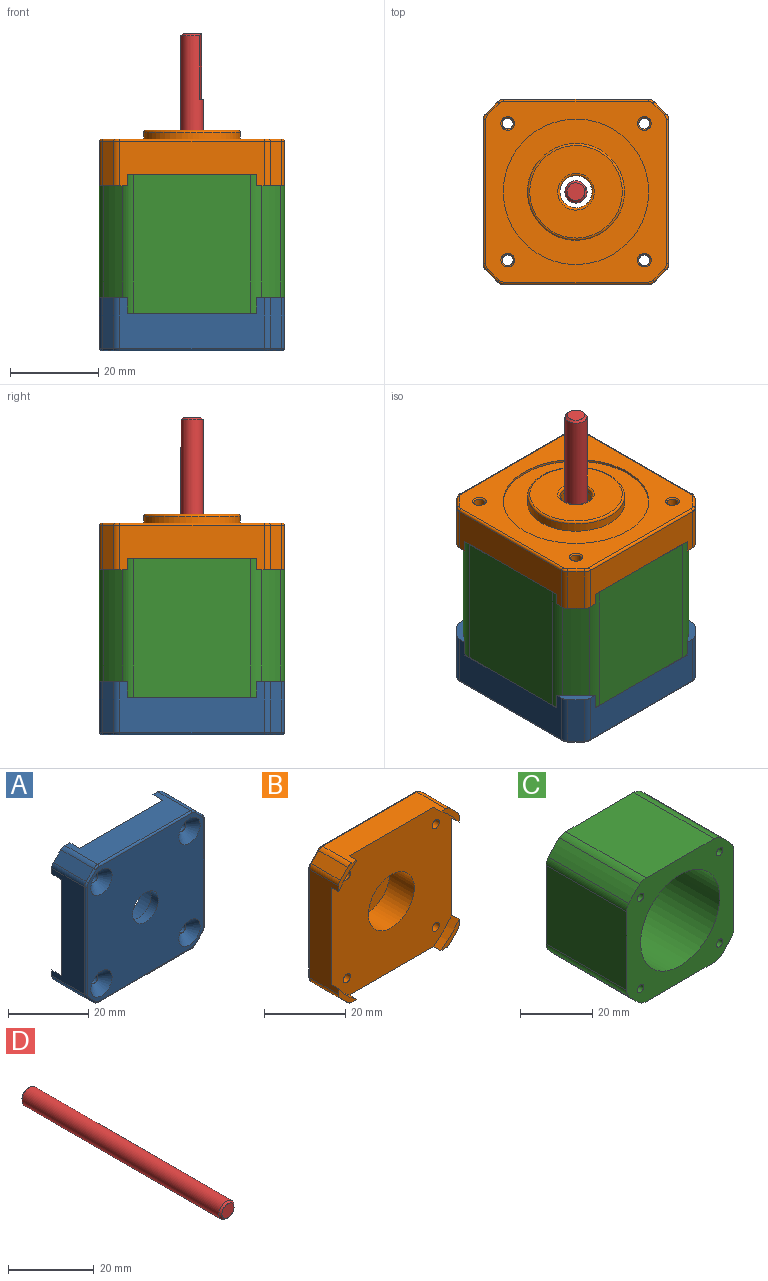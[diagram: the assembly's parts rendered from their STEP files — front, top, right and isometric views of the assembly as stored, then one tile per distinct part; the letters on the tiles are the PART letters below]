
ASSEMBLY  parts=4 mates=8
PART A: 53 faces, bbox 42.3x12x42.3 mm
  f0: cylinder r=4.5mm len=9mm, axis (0,-1,0), area 70.7mm2, adj f10,f28
  f1: plane 32.74x11.5mm, normal (0,0,1), area 274.1mm2, adj f9,f11,f13,f14,f16,f30,f31,f50
  f2: plane 32.74x11.5mm, normal (1,0,0), area 274.1mm2, adj f9,f11,f13,f20,f22,f29,f36,f42
  f3: plane 32.74x11.5mm, normal (0,0,-1), area 274.1mm2, adj f9,f17,f19,f20,f22,f34,f35,f39
  f4: plane 32.74x11.5mm, normal (-1,0,0), area 274.1mm2, adj f9,f14,f16,f17,f19,f32,f33,f47
  f5: cylinder r=1.25mm len=6mm, axis (0,-1,0), area 47.1mm2, adj f9,f26
  f6: cylinder r=1.25mm len=6mm, axis (0,-1,0), area 47.1mm2, adj f9,f25
  f7: cylinder r=1.25mm len=6mm, axis (0,-1,0), area 47.1mm2, adj f9,f24
  f8: cylinder r=1.25mm len=6mm, axis (0,-1,0), area 47.1mm2, adj f9,f23
  f9: plane 42x42mm, normal (0,1,0), area 1472mm2, adj f1,f2,f3,f4,f5,f6,f7,f8
  f10: plane 41x41mm, normal (0,-1,0), area 1415.7mm2, adj f0,f23,f24,f25,f26,f37,f38,f39
  f11: cylinder r=25.6mm len=6.36mm, axis (0,-1,0), area 31.6mm2, adj f1,f2,f9,f13
  f12: plane 11.5x2.63mm, normal (0.71,0,0.71), area 42.7mm2, adj f13,f29,f30,f46
  f13: plane 6.36x6.36mm, normal (0,1,0), area 10.4mm2, adj f1,f2,f11,f12,f29,f30
  f14: cylinder r=25.6mm len=6.36mm, axis (0,-1,0), area 31.6mm2, adj f1,f4,f9,f16
  f15: plane 11.5x2.63mm, normal (-0.71,0,0.71), area 42.7mm2, adj f16,f31,f32,f51
  f16: plane 6.36x6.36mm, normal (0,1,0), area 10.4mm2, adj f1,f4,f14,f15,f31,f32
  f17: cylinder r=25.6mm len=6.36mm, axis (0,-1,0), area 31.6mm2, adj f3,f4,f9,f19
  f18: plane 11.5x2.63mm, normal (-0.71,0,-0.71), area 42.7mm2, adj f19,f33,f34,f43
  f19: plane 6.36x6.36mm, normal (0,1,0), area 10.4mm2, adj f3,f4,f17,f18,f33,f34
  f20: cylinder r=25.6mm len=6.36mm, axis (0,-1,0), area 31.6mm2, adj f2,f3,f9,f22
  f21: plane 11.5x2.63mm, normal (0.71,0,-0.71), area 42.7mm2, adj f22,f35,f36,f38
  f22: plane 6.36x6.36mm, normal (0,1,0), area 10.4mm2, adj f2,f3,f20,f21,f35,f36
  f23: cone r=3.75mm half-angle=45deg, axis (0,-1,0), area 55.5mm2, adj f8,f10
  f24: cone r=3.75mm half-angle=45deg, axis (0,-1,0), area 55.5mm2, adj f7,f10
  f25: cone r=3.75mm half-angle=45deg, axis (0,-1,0), area 55.5mm2, adj f6,f10
  f26: cone r=3.75mm half-angle=45deg, axis (0,-1,0), area 55.5mm2, adj f5,f10
  f27: cylinder r=8mm len=16mm, axis (0,1,0), area 301.6mm2, adj f9,f28
  f28: plane 16x16mm, normal (0,1,0), area 137.4mm2, adj f0,f27
  f29: cylinder r=2mm len=11.5mm, axis (0,-1,0), area 18.1mm2, adj f2,f12,f13,f44
  f30: cylinder r=2mm len=11.5mm, axis (0,-1,0), area 18.1mm2, adj f1,f12,f13,f48
  f31: cylinder r=2mm len=11.5mm, axis (0,-1,0), area 18.1mm2, adj f1,f15,f16,f52
  f32: cylinder r=2mm len=11.5mm, axis (0,1,0), area 18.1mm2, adj f4,f15,f16,f49
  f33: cylinder r=2mm len=11.5mm, axis (0,-1,0), area 18.1mm2, adj f4,f18,f19,f45
  f34: cylinder r=2mm len=11.5mm, axis (0,-1,0), area 18.1mm2, adj f3,f18,f19,f41
  f35: cylinder r=2mm len=11.5mm, axis (0,-1,0), area 18.1mm2, adj f3,f21,f22,f37
  f36: cylinder r=2mm len=11.5mm, axis (0,1,0), area 18.1mm2, adj f2,f21,f22,f40
  f37: torus R=1.5mm, axis (0,1,0), area 1.1mm2, adj f10,f35,f38,f39
  f38: cylinder r=0.5mm len=2.98mm, axis (-0.71,0,-0.71), area 2.9mm2, adj f10,f21,f37,f40
  f39: cylinder r=0.5mm len=32.74mm, axis (-1,0,0), area 25.7mm2, adj f3,f10,f37,f41
  f40: torus R=1.5mm, axis (0,1,0), area 1.1mm2, adj f10,f36,f38,f42
  f41: torus R=1.5mm, axis (0,1,0), area 1.1mm2, adj f10,f34,f39,f43
  f42: cylinder r=0.5mm len=32.74mm, axis (0,0,-1), area 25.7mm2, adj f2,f10,f40,f44
  f43: cylinder r=0.5mm len=2.98mm, axis (-0.71,0,0.71), area 2.9mm2, adj f10,f18,f41,f45
  f44: torus R=1.5mm, axis (0,1,0), area 1.1mm2, adj f10,f29,f42,f46
  f45: torus R=1.5mm, axis (0,1,0), area 1.1mm2, adj f10,f33,f43,f47
  f46: cylinder r=0.5mm len=2.98mm, axis (0.71,0,-0.71), area 2.9mm2, adj f10,f12,f44,f48
  f47: cylinder r=0.5mm len=32.74mm, axis (0,0,1), area 25.7mm2, adj f4,f10,f45,f49
  f48: torus R=1.5mm, axis (0,1,0), area 1.1mm2, adj f10,f30,f46,f50
  f49: torus R=1.5mm, axis (0,1,0), area 1.1mm2, adj f10,f32,f47,f51
  f50: cylinder r=0.5mm len=32.74mm, axis (1,0,0), area 25.7mm2, adj f1,f10,f48,f52
  f51: cylinder r=0.5mm len=2.98mm, axis (0.71,0,0.71), area 2.9mm2, adj f10,f15,f49,f52
  f52: torus R=1.5mm, axis (0,1,0), area 1.1mm2, adj f10,f31,f50,f51
PART B: 59 faces, bbox 42.3x12.6x42.3 mm
  f0: cylinder r=3.65mm len=7.3mm, axis (0,-1,0), area 20.6mm2, adj f28,f53
  f1: plane 42x42mm, normal (0,-1,0), area 1472mm2, adj f2,f4,f6,f8,f9,f10,f11,f14
  f2: plane 32.74x10.1mm, normal (0,0,1), area 254.6mm2, adj f1,f19,f20,f21,f22,f30,f31,f51
  f3: plane 10.1x2.63mm, normal (0.71,0,0.71), area 37.5mm2, adj f22,f29,f30,f47
  f4: plane 32.74x10.1mm, normal (1,0,0), area 254.6mm2, adj f1,f21,f22,f25,f26,f29,f36,f43
  f5: plane 10.1x2.63mm, normal (0.71,0,-0.71), area 37.5mm2, adj f26,f35,f36,f39
  f6: plane 32.74x10.1mm, normal (0,0,-1), area 254.6mm2, adj f1,f23,f24,f25,f26,f34,f35,f38
  f7: plane 10.1x2.63mm, normal (-0.71,0,-0.71), area 37.5mm2, adj f24,f33,f34,f42
  f8: plane 32.74x10.1mm, normal (-1,0,0), area 254.6mm2, adj f1,f19,f20,f23,f24,f32,f33,f46
  f9: cylinder r=1.25mm len=7.7mm, axis (0,-1,0), area 60.5mm2, adj f1,f58
  f10: cylinder r=1.25mm len=7.7mm, axis (0,-1,0), area 60.5mm2, adj f1,f57
  f11: cylinder r=1.25mm len=7.7mm, axis (0,-1,0), area 60.5mm2, adj f1,f56
  f12: plane 10.1x2.63mm, normal (-0.71,0,0.71), area 37.5mm2, adj f20,f31,f32,f50
  f13: cylinder r=16.5mm len=33mm, axis (0,-1,0), area 51.8mm2, adj f15,f16
  f14: cylinder r=1.25mm len=7.7mm, axis (0,-1,0), area 60.5mm2, adj f1,f55
  f15: plane 41x41mm, normal (0,1,0), area 770.5mm2, adj f13,f37,f38,f39,f40,f41,f42,f43
  f16: plane 33x33mm, normal (0,1,0), area 475.2mm2, adj f13,f17
  f17: cylinder r=11mm len=22mm, axis (0,-1,0), area 138.2mm2, adj f16,f54
  f18: plane 21x21mm, normal (0,1,0), area 292.3mm2, adj f53,f54
  f19: cylinder r=25.6mm len=6.36mm, axis (0,1,0), area 23.5mm2, adj f1,f2,f8,f20
  f20: plane 6.36x6.36mm, normal (0,-1,0), area 10.4mm2, adj f2,f8,f12,f19,f31,f32
  f21: cylinder r=25.6mm len=6.36mm, axis (0,1,0), area 23.5mm2, adj f1,f2,f4,f22
  f22: plane 6.36x6.36mm, normal (0,-1,0), area 10.4mm2, adj f2,f3,f4,f21,f29,f30
  f23: cylinder r=25.6mm len=6.36mm, axis (0,1,0), area 23.5mm2, adj f1,f6,f8,f24
  f24: plane 6.36x6.36mm, normal (0,-1,0), area 10.4mm2, adj f6,f7,f8,f23,f33,f34
  f25: cylinder r=25.6mm len=6.36mm, axis (0,1,0), area 23.5mm2, adj f1,f4,f6,f26
  f26: plane 6.36x6.36mm, normal (0,-1,0), area 10.4mm2, adj f4,f5,f6,f25,f35,f36
  f27: cylinder r=8mm len=16mm, axis (0,-1,0), area 432.3mm2, adj f1,f28
  f28: plane 16x16mm, normal (0,-1,0), area 159.2mm2, adj f0,f27
  f29: cylinder r=2mm len=10.1mm, axis (0,-1,0), area 15.9mm2, adj f3,f4,f22,f45
  f30: cylinder r=2mm len=10.1mm, axis (0,-1,0), area 15.9mm2, adj f2,f3,f22,f49
  f31: cylinder r=2mm len=10.1mm, axis (0,-1,0), area 15.9mm2, adj f2,f12,f20,f52
  f32: cylinder r=2mm len=10.1mm, axis (0,1,0), area 15.9mm2, adj f8,f12,f20,f48
  f33: cylinder r=2mm len=10.1mm, axis (0,-1,0), area 15.9mm2, adj f7,f8,f24,f44
  f34: cylinder r=2mm len=10.1mm, axis (0,-1,0), area 15.9mm2, adj f6,f7,f24,f40
  f35: cylinder r=2mm len=10.1mm, axis (0,-1,0), area 15.9mm2, adj f5,f6,f26,f37
  f36: cylinder r=2mm len=10.1mm, axis (0,1,0), area 15.9mm2, adj f4,f5,f26,f41
  f37: torus R=1.5mm, axis (0,1,0), area 1.1mm2, adj f15,f35,f38,f39
  f38: cylinder r=0.5mm len=32.74mm, axis (1,0,0), area 25.7mm2, adj f6,f15,f37,f40
  f39: cylinder r=0.5mm len=2.98mm, axis (0.71,0,0.71), area 2.9mm2, adj f5,f15,f37,f41
  f40: torus R=1.5mm, axis (0,1,0), area 1.1mm2, adj f15,f34,f38,f42
  f41: torus R=1.5mm, axis (0,1,0), area 1.1mm2, adj f15,f36,f39,f43
  f42: cylinder r=0.5mm len=2.98mm, axis (0.71,0,-0.71), area 2.9mm2, adj f7,f15,f40,f44
  f43: cylinder r=0.5mm len=32.74mm, axis (0,0,1), area 25.7mm2, adj f4,f15,f41,f45
  f44: torus R=1.5mm, axis (0,1,0), area 1.1mm2, adj f15,f33,f42,f46
  f45: torus R=1.5mm, axis (0,1,0), area 1.1mm2, adj f15,f29,f43,f47
  f46: cylinder r=0.5mm len=32.74mm, axis (0,0,-1), area 25.7mm2, adj f8,f15,f44,f48
  f47: cylinder r=0.5mm len=2.98mm, axis (-0.71,0,0.71), area 2.9mm2, adj f3,f15,f45,f49
  f48: torus R=1.5mm, axis (0,1,0), area 1.1mm2, adj f15,f32,f46,f50
  f49: torus R=1.5mm, axis (0,1,0), area 1.1mm2, adj f15,f30,f47,f51
  f50: cylinder r=0.5mm len=2.98mm, axis (-0.71,0,-0.71), area 2.9mm2, adj f12,f15,f48,f52
  f51: cylinder r=0.5mm len=32.74mm, axis (-1,0,0), area 25.7mm2, adj f2,f15,f49,f52
  f52: torus R=1.5mm, axis (0,1,0), area 1.1mm2, adj f15,f31,f50,f51
  f53: torus R=4.15mm, axis (0,1,0), area 18.9mm2, adj f0,f18
  f54: torus R=10.5mm, axis (0,1,0), area 53.4mm2, adj f17,f18
  f55: cone r=1.25mm half-angle=45deg, axis (0,1,0), area 3.7mm2, adj f14,f15
  f56: cone r=1.25mm half-angle=45deg, axis (0,1,0), area 3.7mm2, adj f11,f15
  f57: cone r=1.25mm half-angle=45deg, axis (0,1,0), area 3.7mm2, adj f10,f15
  f58: cone r=1.25mm half-angle=45deg, axis (0,1,0), area 3.7mm2, adj f9,f15
PART C: 23 faces, bbox 42x31.5x42 mm
  f0: plane 42x42mm, normal (0,1,0), area 916.8mm2, adj f1,f2,f3,f4,f5,f6,f7,f8
  f1: cylinder r=25.6mm len=31.5mm, axis (0,-1,0), area 194.5mm2, adj f0,f16,f17,f22
  f2: plane 31.5x26.65mm, normal (0,0,-1), area 839.5mm2, adj f0,f15,f16,f22
  f3: cylinder r=25.6mm len=31.5mm, axis (0,-1,0), area 194.5mm2, adj f0,f14,f15,f22
  f4: plane 31.5x26.65mm, normal (-1,0,0), area 839.5mm2, adj f0,f14,f21,f22
  f5: cylinder r=25.6mm len=31.5mm, axis (0,-1,0), area 194.5mm2, adj f0,f20,f21,f22
  f6: plane 31.5x26.65mm, normal (0,0,1), area 839.5mm2, adj f0,f19,f20,f22
  f7: cylinder r=25.6mm len=31.5mm, axis (0,-1,0), area 194.5mm2, adj f0,f18,f19,f22
  f8: plane 31.5x26.65mm, normal (1,0,0), area 839.5mm2, adj f0,f17,f18,f22
  f9: cylinder r=15.5mm len=31.5mm, axis (0,-1,0), area 3067.8mm2, adj f0,f22
  f10: cylinder r=1.25mm len=31.5mm, axis (0,-1,0), area 247.4mm2, adj f0,f22
  f11: cylinder r=1.25mm len=31.5mm, axis (0,-1,0), area 247.4mm2, adj f0,f22
  f12: cylinder r=1.25mm len=31.5mm, axis (0,-1,0), area 247.4mm2, adj f0,f22
  f13: cylinder r=1.25mm len=31.5mm, axis (0,-1,0), area 247.4mm2, adj f0,f22
  f14: cylinder r=4mm len=31.5mm, axis (0,-1,0), area 83.8mm2, adj f0,f3,f4,f22
  f15: cylinder r=4mm len=31.5mm, axis (0,-1,0), area 83.8mm2, adj f0,f2,f3,f22
  f16: cylinder r=4mm len=31.5mm, axis (0,-1,0), area 83.8mm2, adj f0,f1,f2,f22
  f17: cylinder r=4mm len=31.5mm, axis (0,-1,0), area 83.8mm2, adj f0,f1,f8,f22
  f18: cylinder r=4mm len=31.5mm, axis (0,-1,0), area 83.8mm2, adj f0,f7,f8,f22
  f19: cylinder r=4mm len=31.5mm, axis (0,-1,0), area 83.8mm2, adj f0,f6,f7,f22
  f20: cylinder r=4mm len=31.5mm, axis (0,-1,0), area 83.8mm2, adj f0,f5,f6,f22
  f21: cylinder r=4mm len=31.5mm, axis (0,-1,0), area 83.8mm2, adj f0,f4,f5,f22
  f22: plane 42x42mm, normal (0,-1,0), area 916.8mm2, adj f1,f2,f3,f4,f5,f6,f7,f8
PART D: 7 faces, bbox 5x66x5 mm
  f0: cylinder r=2.5mm len=65mm, axis (0,-1,0), area 974.4mm2, adj f2,f3,f4,f6
  f1: plane 4x4mm, normal (0,1,0), area 12.6mm2, adj f4
  f2: plane 15x3mm, normal (0,0,-1), area 44.5mm2, adj f0,f3,f4
  f3: plane 3x0.5mm, normal (0,1,0), area 1mm2, adj f0,f2
  f4: cone r=2mm half-angle=45deg, axis (0,-1,0), area 8.6mm2, adj f0,f1,f2
  f5: plane 4x4mm, normal (0,-1,0), area 12.6mm2, adj f6
  f6: cone r=2.5mm half-angle=45deg, axis (0,1,0), area 10mm2, adj f0,f5
PLACE A rot(axis=(0.58,0.58,0.58),120deg) t=(0,0,0)mm fixed
PLACE B rot(axis=(0.58,-0.58,-0.58),120deg) t=(0,0,40)mm
PLACE C rot(axis=(0.58,-0.58,-0.58),120deg) t=(0,0,24)mm
PLACE D rot(axis=(0.53,-0.6,-0.6),124.4deg) t=(0,0,6)mm
MATE parallel C.f2 <-> A.f1  axis (1,0,0) through (21,0,24.25)mm
MATE cylindrical D.f0 <-> B.f0  axis (0,0,-1) through (0,0,39)mm
MATE planar C.f0 <-> B.f27  axis (0,0,1) through (-21,0,40)mm
MATE cylindrical C.f1 <-> B.f27  axis (0,0,-1) through (0,0,24.25)mm
MATE planar C.f21 <-> A.f0  axis (0,0,-1) through (-13.33,17,8.5)mm
MATE planar D.f0 <-> B.f27  axis (0,0,1) through (0,0,72)mm
MATE parallel B.f2 <-> C.f6  axis (-1,0,0) through (-21,0,43.57)mm
MATE cylindrical C.f1 <-> A.f0  axis (0,0,-1) through (0,0,8.5)mm
